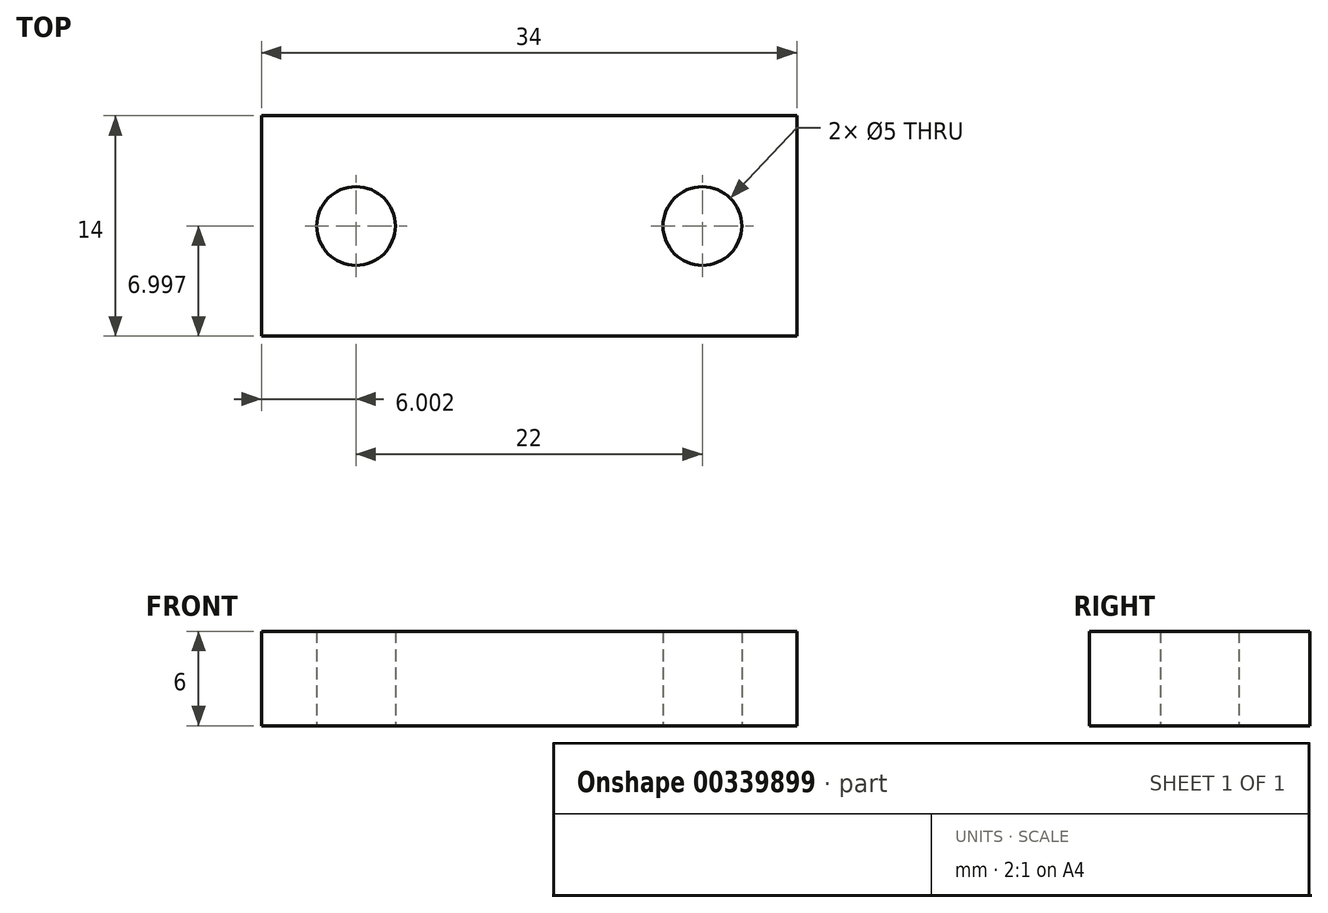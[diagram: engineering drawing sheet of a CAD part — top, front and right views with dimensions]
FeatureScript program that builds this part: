
annotation { "Feature Type Name" : "Feature", "Feature Type Description" : "" }
export const myFeature = defineFeature(function(context is Context, id is Id, definition is map)
    precondition{}
    {
        {
            var Q0;
            Q0=qCreatedBy(makeId("Top.planeOp"),FACE);
            var sketch = newSketch(context, id + "F0", { "sketchPlane" : qUnion([Q0])});
            skLineSegment(sketch, "E0.bottom", {"start": v(10.21, 4.58) * mm, "end": v(44.21, 4.58) * mm});
            skLineSegment(sketch, "E0.top", {"start": v(10.21, -9.42) * mm, "end": v(44.21, -9.42) * mm});
            skLineSegment(sketch, "E0.left", {"start": v(10.21, 4.58) * mm, "end": v(10.21, -9.42) * mm});
            skLineSegment(sketch, "E0.right", {"start": v(44.21, 4.58) * mm, "end": v(44.21, -9.42) * mm});
            skLineSegment(sketch, "E1", {"start": v(10.21, -2.42) * mm, "end": v(44.21, -2.42) * mm, "construction": true});
            skCircle(sketch, "E2", {"center": v(16.21, -2.42) * mm, "radius": 2.5 * mm});
            skCircle(sketch, "E3", {"center": v(38.21, -2.42) * mm, "radius": 2.5 * mm});
            skSolve(sketch);
        }
        {
            var Q0;
            Q0 = qSketchRegion(id + "F0", true);
            extrude(context, id + "F1", {"entities" : qUnion([Q0]), "depth" : 6 * mm, "offsetDistance" : 25 * mm});
        }
    });
